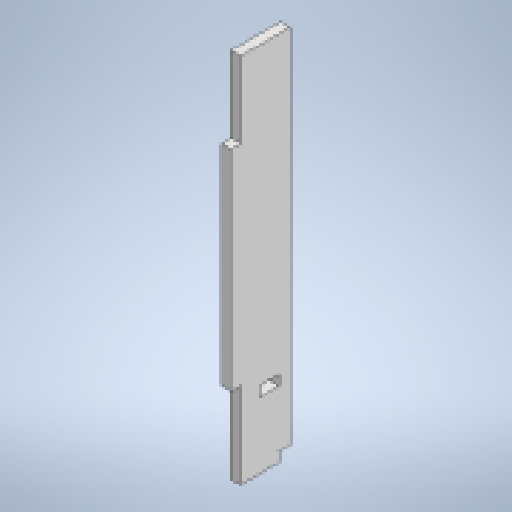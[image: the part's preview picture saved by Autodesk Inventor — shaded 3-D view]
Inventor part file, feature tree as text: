
AUTODESK INVENTOR PART (.ipt)
format: ipt  version: 2023 (Build 270158000, 158)  size: 188,416 bytes
history: native  units: mm
features: extrude x5, sketch x5, reference x3, other x3
ambient origin geometry x8: Origin, YZ Plane, XZ Plane, XY Plane, X Axis, Y Axis, Z Axis, Center Point
bodies: Solid1 (feature_tree)
feature tree (16):
  extrude  "Extrusion1"  Depth=31.0mm
  extrude  "Extrusion2"  Depth=5.0mm
  extrude  "Extrusion3"  Depth=5.0mm
  extrude  "Extrusion4"  Depth=5.0mm
  extrude  "Extrusion5"  Depth=5.0mm
  sketch  "Sketch1"  dims[d0=31.0mm d1=200.0mm]
  sketch  "Sketch2"  dims[d2=5.0mm d3=0.0mm d4=5.0mm]
  sketch  "Sketch3"  dims[d5=5.0mm d6=5.0mm]
  reference  "Reference1"
  reference  "Reference2"
  reference  "Reference3"
  sketch  "Sketch4"  dims[d7=5.0mm d8=5.0mm]
  sketch  "Sketch5"  dims[d9=5.0mm d10=5.0mm d11=5.0mm d12=10.0mm d13=0.0mm d14=40.0mm d15=40.0mm d16=10.0mm d17=0.0mm d18=5.0mm d19=10.0mm d20=0.0mm d21=6.0mm d22=5.0mm d23=6.0mm d24=10.0mm d25=0.0mm]
  other  "<userpath>\OneDrive\ClawdDrive\Objet3D\Clawd4\Assembly1.iam"
  other  "Assembly1.iam"
  other  "FANsuport:2"
